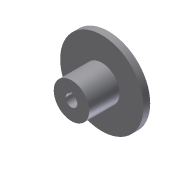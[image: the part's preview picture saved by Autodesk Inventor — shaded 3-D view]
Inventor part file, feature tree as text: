
AUTODESK INVENTOR PART (.ipt)
format: ipt  version: 2013 (Build 170138000, 138)  size: 94,208 bytes
history: native  units: in
note: dims shown in document units (in); Inventor stores cm internally (conversion verified against a paired STEP export)
features: extrude x3, sketch x3
ambient origin geometry x8: Origin, YZ Plane, XZ Plane, XY Plane, X Axis, Y Axis, Z Axis, Center Point
bodies: Solid1 (feature_tree)
feature tree (6):
  extrude  "Extrusion1"  Depth=0.18in TaperAngle=0.0deg
  extrude  "Extrusion2"  Depth=0.82in TaperAngle=0.0deg
  extrude  "Extrusion3"  Depth=0.0787in
  sketch  "Sketch1"  dims[d0=2.25in d1=0.18in d2=0.0in]
  sketch  "Sketch2"  dims[d3=0.958in d4=0.82in d5=0.0in]
  sketch  "Sketch3"  dims[d6=0.315in d7=0.0787in d8=0.0787in d9=0.82in d10=0.0in]
